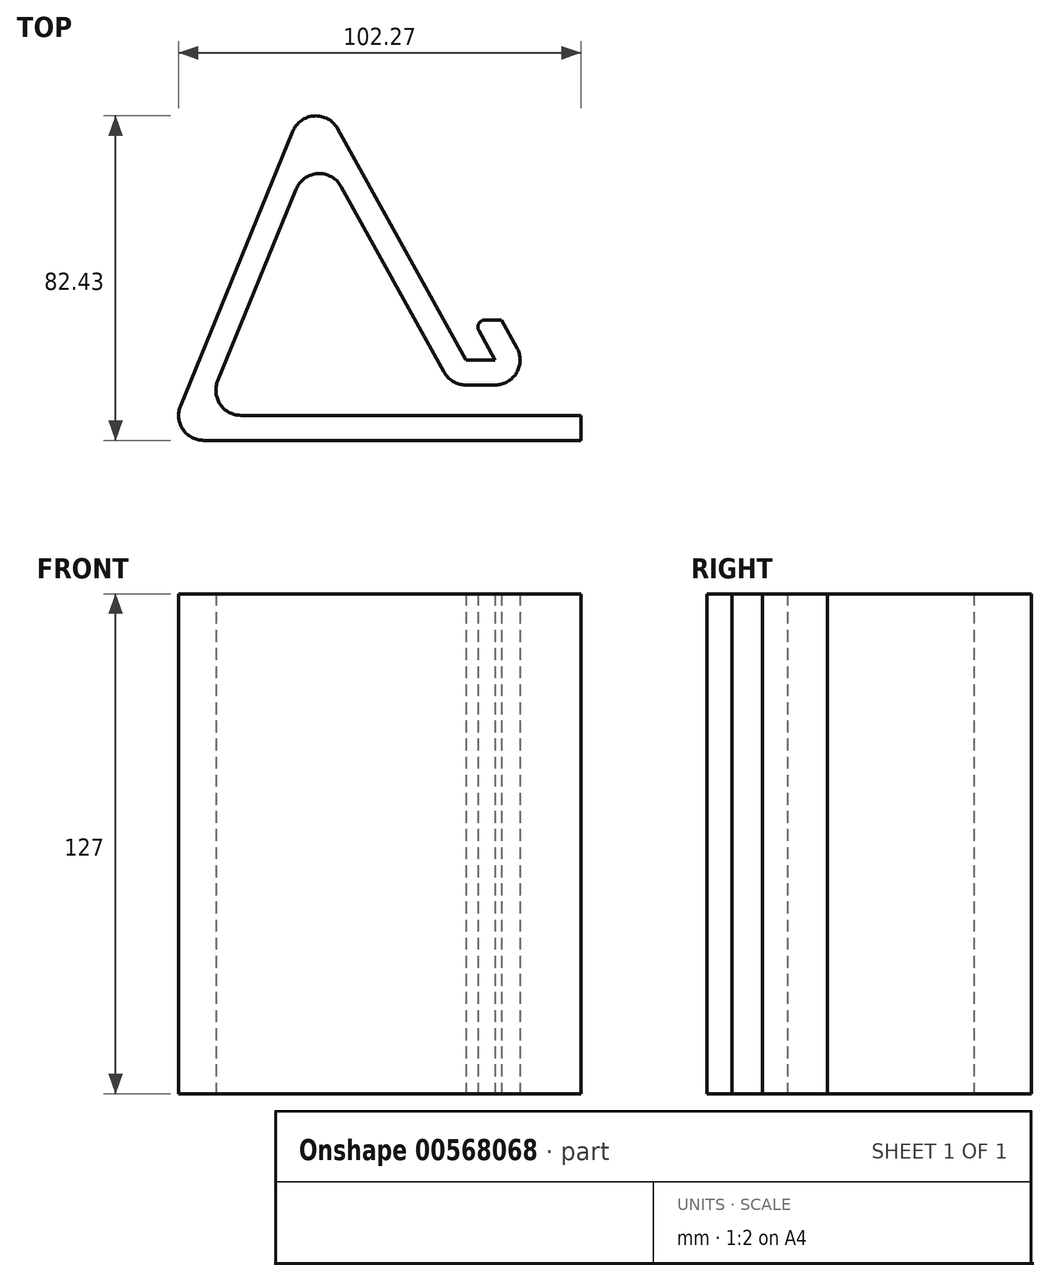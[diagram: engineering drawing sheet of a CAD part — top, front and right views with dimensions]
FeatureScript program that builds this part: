
annotation { "Feature Type Name" : "Feature", "Feature Type Description" : "" }
export const myFeature = defineFeature(function(context is Context, id is Id, definition is map)
    precondition{}
    {
        {
            var Q0;
            Q0=qCreatedBy(makeId("Top.planeOp"),FACE);
            var sketch = newSketch(context, id + "F0", { "sketchPlane" : qUnion([Q0])});
            skLineSegment(sketch, "E0", {"start": v(57.95, -44.75) * mm, "end": v(-37.97, -44.75) * mm});
            skLineSegment(sketch, "E1", {"start": v(-43.85, -36) * mm, "end": v(-15.32, 33.73) * mm});
            skLineSegment(sketch, "E2", {"start": v(-3.9, 34.4) * mm, "end": v(28.66, -24.33) * mm});
            skLineSegment(sketch, "E3", {"start": v(28.66, -24.33) * mm, "end": v(36.09, -24.33) * mm});
            skLineSegment(sketch, "E4", {"start": v(36.09, -24.33) * mm, "end": v(31.97, -16.9) * mm});
            skLineSegment(sketch, "E5.0", {"start": v(41.64, -21.25) * mm, "end": v(37.7, -14.15) * mm});
            skLineSegment(sketch, "E5.1", {"start": v(57.95, -38.4) * mm, "end": v(-28.51, -38.4) * mm});
            skLineSegment(sketch, "E5.2", {"start": v(-34.39, -29.64) * mm, "end": v(-14.46, 19.07) * mm});
            skLineSegment(sketch, "E5.3", {"start": v(-3.03, 19.75) * mm, "end": v(23.1, -27.41) * mm});
            skLineSegment(sketch, "E5.4", {"start": v(28.66, -30.68) * mm, "end": v(36.09, -30.68) * mm});
            skLineSegment(sketch, "E6", {"start": v(33.58, -14.15) * mm, "end": v(37.7, -14.15) * mm});
            skLineSegment(sketch, "E7", {"start": v(57.95, -44.75) * mm, "end": v(57.95, -38.4) * mm});
            skPoint(sketch, "E8.visualSharp", {"position": v(-10.31, 45.99) * mm});
            skArc(sketch, "E8.filletArc", {"start": v(-3.9, 34.4) * mm, "mid": v(-9.82, 37.67) * mm, "end": v(-15.32, 33.73) * mm});
            skArc(sketch, "E9.filletArc", {"start": v(-3.03, 19.75) * mm, "mid": v(-8.96, 23) * mm, "end": v(-14.46, 19.07) * mm});
            skPoint(sketch, "E10.visualSharp", {"position": v(-37.97, -38.4) * mm});
            skArc(sketch, "E10.filletArc", {"start": v(-34.39, -29.64) * mm, "mid": v(-33.78, -35.59) * mm, "end": v(-28.51, -38.4) * mm});
            skPoint(sketch, "E11.visualSharp", {"position": v(-47.43, -44.75) * mm});
            skArc(sketch, "E11.filletArc", {"start": v(-43.85, -36) * mm, "mid": v(-43.24, -41.94) * mm, "end": v(-37.97, -44.75) * mm});
            skPoint(sketch, "E12.visualSharp", {"position": v(24.92, -30.68) * mm});
            skArc(sketch, "E12.filletArc", {"start": v(23.1, -27.41) * mm, "mid": v(25.44, -29.8) * mm, "end": v(28.66, -30.68) * mm});
            skPoint(sketch, "E13.visualSharp", {"position": v(46.87, -30.68) * mm});
            skArc(sketch, "E13.filletArc", {"start": v(36.09, -30.68) * mm, "mid": v(41.56, -27.56) * mm, "end": v(41.64, -21.25) * mm});
            skPoint(sketch, "E14.visualSharp", {"position": v(30.45, -14.15) * mm});
            skArc(sketch, "E14.filletArc", {"start": v(33.58, -14.15) * mm, "mid": v(31.99, -15.06) * mm, "end": v(31.97, -16.9) * mm});
            skSolve(sketch);
        }
        {
            var Q0;
            Q0=makeQuery(id+"F0.imprint","IMPRINT",FACE,{"disambiguationData":[TD([[makeQuery(id+"F0.imprint","IMPRINT",EDGE,{"derivedFrom":sQuery(id+"F0.wireOp",EDGE,"E0")}),-1.0]])]});
            extrude(context, id + "F1", {"entities" : qUnion([Q0]), "depth" : 127 * mm, "offsetDistance" : 25.4 * mm});
        }
    });
